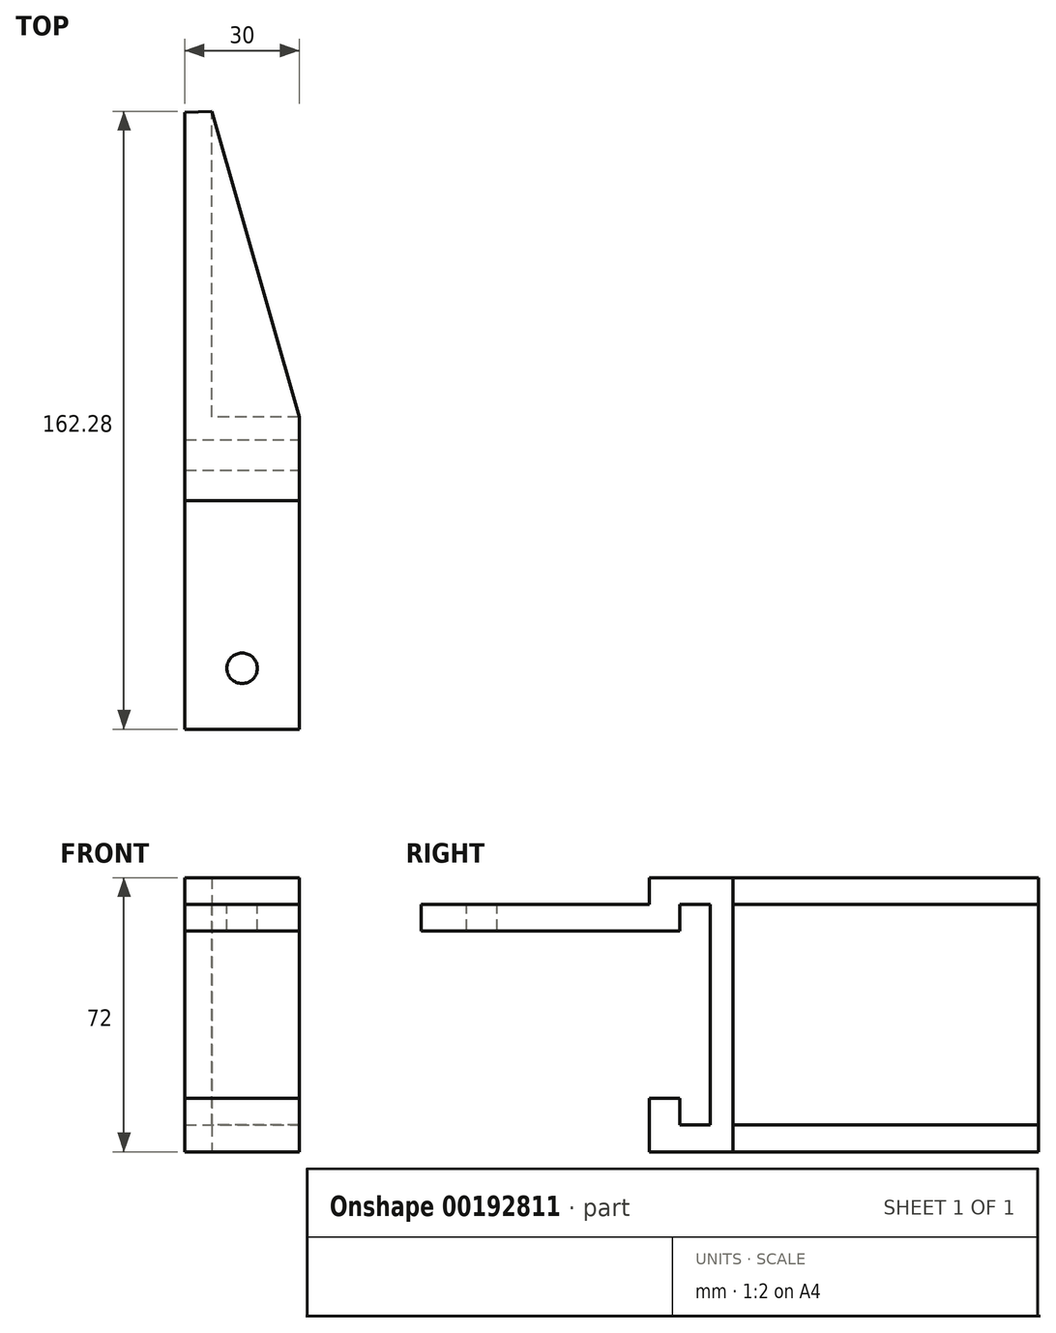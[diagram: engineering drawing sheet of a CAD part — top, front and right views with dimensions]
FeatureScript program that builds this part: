
annotation { "Feature Type Name" : "Feature", "Feature Type Description" : "" }
export const myFeature = defineFeature(function(context is Context, id is Id, definition is map)
    precondition{}
    {
        {
            var Q0;
            Q0=qCreatedBy(makeId("Top.planeOp"),FACE);
            var sketch = newSketch(context, id + "F0", { "sketchPlane" : qUnion([Q0])});
            skLineSegment(sketch, "E0.bottom", {"start": v(0, 0) * mm, "end": v(30, 0) * mm});
            skLineSegment(sketch, "E0.top", {"start": v(0, 22) * mm, "end": v(30, 22) * mm});
            skLineSegment(sketch, "E0.left", {"start": v(30, 0) * mm, "end": v(30, 22) * mm});
            skLineSegment(sketch, "E0.right", {"start": v(0, 0) * mm, "end": v(0, 22) * mm});
            skLineSegment(sketch, "E1", {"start": v(0, 22) * mm, "end": v(0, 102) * mm});
            skLineSegment(sketch, "E2", {"start": v(30, 22) * mm, "end": v(7, 102.28) * mm});
            skLineSegment(sketch, "E3", {"start": v(0, 102) * mm, "end": v(7, 102.28) * mm});
            skSolve(sketch);
        }
        {
            var Q0;
            Q0=qSketchRegion(id+"F0",true);
            extrude(context, id + "F1", {"entities" : qUnion([Q0]), "depth" : 72 * mm});
        }
        {
            var Q0;
            Q0=makeQuery(id+"F1.opExtrude","CAP_FACE",FACE,{"disambiguationData":[OSD([sQuery(id+"F0.wireOp",EDGE,"E0.bottom"),sQuery(id+"F0.wireOp",EDGE,"E0.left"),sQuery(id+"F0.wireOp",EDGE,"E0.right"),sQuery(id+"F0.wireOp",EDGE,"E1"),sQuery(id+"F0.wireOp",EDGE,"xLnjd96q-PZ0L-wumJ-MDfw-arIAMcblvKvu")])],"isStart":false});
            var sketch = newSketch(context, id + "F2", { "sketchPlane" : qUnion([Q0])});
            skLineSegment(sketch, "E4", {"start": v(30, 22) * mm, "end": v(7, 22) * mm});
            skLineSegment(sketch, "E5", {"start": v(7, 22) * mm, "end": v(7, 102.28) * mm});
            skLineSegment(sketch, "E6", {"start": v(7, 102.28) * mm, "end": v(30, 22) * mm});
            skSolve(sketch);
        }
        {
            var Q0;
            Q0=qSketchRegion(id+"F2",true);
            extrude(context, id + "F3", {"entities" : qUnion([Q0]), "operationType" : NewBodyOperationType.REMOVE, "endBound" : BoundingType.THROUGH_ALL, "oppositeDirection" : true, "depth" : 25 * mm});
        }
        {
            var Q0;
            Q0=qSketchRegion(id+"F2",true);
            extrude(context, id + "F4", {"entities" : qUnion([Q0]), "operationType" : NewBodyOperationType.ADD, "oppositeDirection" : true, "depth" : 7 * mm});
        }
        {
            var Q0;
            Q0=makeQuery(id+"F1.opExtrude","CAP_FACE",FACE,{"disambiguationData":[OSD([sQuery(id+"F0.wireOp",EDGE,"E0.bottom"),sQuery(id+"F0.wireOp",EDGE,"E0.left"),sQuery(id+"F0.wireOp",EDGE,"E0.right"),sQuery(id+"F0.wireOp",EDGE,"E1"),sQuery(id+"F0.wireOp",EDGE,"xLnjd96q-PZ0L-wumJ-MDfw-arIAMcblvKvu")])],"isStart":true});
            var sketch = newSketch(context, id + "F5", { "sketchPlane" : qUnion([Q0])});
            skLineSegment(sketch, "E7", {"start": v(53, -22) * mm, "end": v(53, -22) * mm});
            skLineSegment(sketch, "E8", {"start": v(30, -22) * mm, "end": v(7, -102.28) * mm});
            skLineSegment(sketch, "E9", {"start": v(30, -22) * mm, "end": v(7, -22) * mm});
            skLineSegment(sketch, "E10", {"start": v(7, -22) * mm, "end": v(7, -102.28) * mm});
            skSolve(sketch);
        }
        {
            var Q0;
            Q0=qSketchRegion(id+"F5",true);
            extrude(context, id + "F6", {"entities" : qUnion([Q0]), "operationType" : NewBodyOperationType.ADD, "oppositeDirection" : true, "depth" : 7 * mm});
        }
        {
            var Q0;
            Q0=makeQuery(id+"F1.opExtrude","SWEPT_FACE",FACE,{"disambiguationData":[OSD([sQuery(id+"F0.wireOp",EDGE,"E0.left")])]});
            var sketch = newSketch(context, id + "F7", { "sketchPlane" : qUnion([Q0])});
            skLineSegment(sketch, "E11.bottom", {"start": v(8, 65) * mm, "end": v(16, 65) * mm});
            skLineSegment(sketch, "E11.top", {"start": v(8, 7) * mm, "end": v(16, 7) * mm});
            skLineSegment(sketch, "E11.left", {"start": v(16, 7) * mm, "end": v(16, 65) * mm});
            skLineSegment(sketch, "E11.right", {"start": v(8, 7) * mm, "end": v(8, 65) * mm});
            skLineSegment(sketch, "E12.bottom", {"start": v(0, 58) * mm, "end": v(8, 58) * mm});
            skLineSegment(sketch, "E12.top", {"start": v(0, 14) * mm, "end": v(8, 14) * mm});
            skLineSegment(sketch, "E12.left", {"start": v(8, 58) * mm, "end": v(8, 14) * mm});
            skLineSegment(sketch, "E12.right", {"start": v(0, 58) * mm, "end": v(0, 14) * mm});
            skSolve(sketch);
        }
        {
            var Q0;
            Q0=qSketchRegion(id+"F7",true);
            extrude(context, id + "F8", {"entities" : qUnion([Q0]), "operationType" : NewBodyOperationType.REMOVE, "endBound" : BoundingType.THROUGH_ALL, "oppositeDirection" : true, "depth" : 25 * mm});
        }
        {
            var Q0;
            {var subQ3=sQuery(id+"F0.wireOp",EDGE,"E0.bottom");Q0=makeQuery(id+"F8.boolean.opBoolean","SPLIT",FACE,{"disambiguationData":[TD([makeQuery(id+"F8.opExtrude","SWEPT_FACE",FACE,{"disambiguationData":[OSD([sQuery(id+"F7.wireOp",EDGE,"E12.bottom")])]})])],"derivedFrom":makeQuery(id+"F1.opExtrude","SWEPT_FACE",FACE,{"disambiguationData":[OSD([subQ3])]})});}
            var sketch = newSketch(context, id + "F9", { "sketchPlane" : qUnion([Q0])});
            skLineSegment(sketch, "E13.bottom", {"start": v(0, 58) * mm, "end": v(30, 58) * mm});
            skLineSegment(sketch, "E13.top", {"start": v(0, 65) * mm, "end": v(30, 65) * mm});
            skLineSegment(sketch, "E13.left", {"start": v(30, 58) * mm, "end": v(30, 65) * mm});
            skLineSegment(sketch, "E13.right", {"start": v(0, 58) * mm, "end": v(0, 65) * mm});
            skSolve(sketch);
        }
        {
            var Q0;
            Q0=qSketchRegion(id+"F9",true);
            extrude(context, id + "F10", {"entities" : qUnion([Q0]), "operationType" : NewBodyOperationType.ADD, "depth" : 60 * mm});
        }
        {
            var Q0;
            Q0=makeQuery(id+"F10.opExtrude","SWEPT_FACE",FACE,{"disambiguationData":[OSD([sQuery(id+"F9.wireOp",EDGE,"E13.top")])]});
            var sketch = newSketch(context, id + "F11", { "sketchPlane" : qUnion([Q0])});
            skCircle(sketch, "E14", {"center": v(15, -44) * mm, "radius": 4 * mm});
            skPoint(sketch, "E14.centerSnap0", {"position": v(15, -60) * mm});
            skSolve(sketch);
        }
        {
            var Q0;
            Q0=qSketchRegion(id+"F11",true);
            extrude(context, id + "F12", {"entities" : qUnion([Q0]), "operationType" : NewBodyOperationType.REMOVE, "endBound" : BoundingType.THROUGH_ALL, "oppositeDirection" : true, "depth" : 25 * mm});
        }
    });
